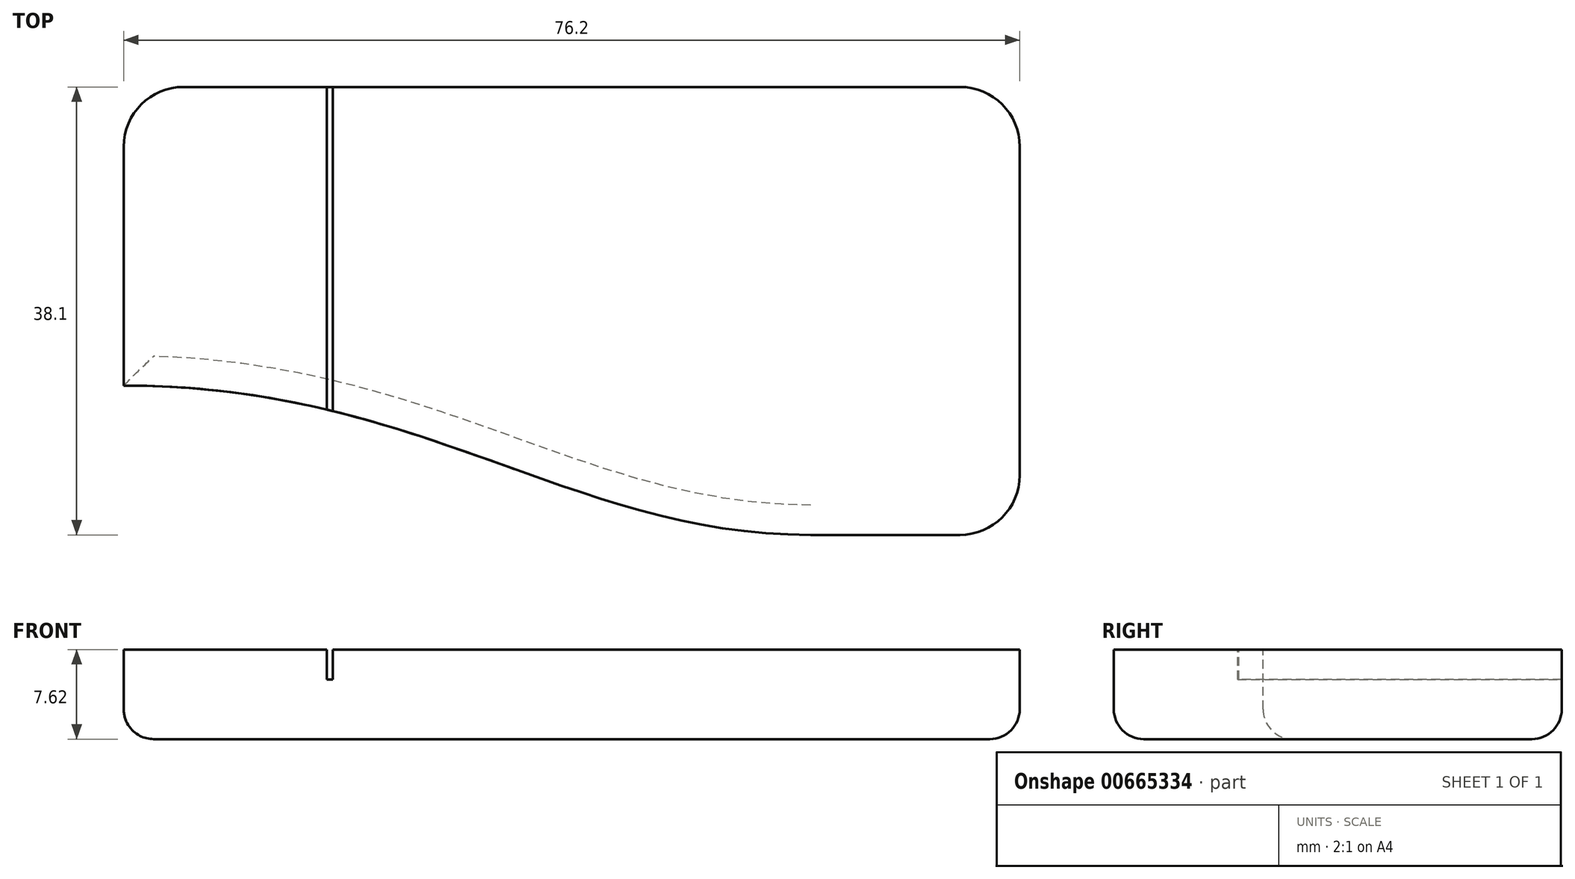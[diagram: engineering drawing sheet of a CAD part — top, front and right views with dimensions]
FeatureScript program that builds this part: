
annotation { "Feature Type Name" : "Feature", "Feature Type Description" : "" }
export const myFeature = defineFeature(function(context is Context, id is Id, definition is map)
    precondition{}
    {
        {
            var Q0;
            Q0=qCreatedBy(makeId("Top.planeOp"),FACE);
            var sketch = newSketch(context, id + "F0", { "sketchPlane" : qUnion([Q0])});
            skLineSegment(sketch, "E0.bottom", {"start": v(38.1, -19.05) * mm, "end": v(-38.1, -19.05) * mm});
            skLineSegment(sketch, "E0.top", {"start": v(38.1, 19.05) * mm, "end": v(-38.1, 19.05) * mm});
            skLineSegment(sketch, "E0.left", {"start": v(38.1, -19.05) * mm, "end": v(38.1, 19.05) * mm});
            skLineSegment(sketch, "E0.right", {"start": v(-38.1, -19.05) * mm, "end": v(-38.1, 19.05) * mm});
            skPoint(sketch, "E0.middle", {"position": v(0, 0) * mm});
            skSolve(sketch);
        }
        {
            var Q0;
            Q0=makeQuery(id+"F0.imprint","IMPRINT",FACE,{"disambiguationData":[TD([[makeQuery(id+"F0.imprint","IMPRINT",EDGE,{"derivedFrom":sQuery(id+"F0.wireOp",EDGE,"E0.bottom")}),-1.0]])]});
            extrude(context, id + "F1", {"entities" : qUnion([Q0]), "depth" : 7.62 * mm, "offsetDistance" : 25.4 * mm});
        }
        {
            var Q0;
            Q0=makeQuery(id+"F1.opExtrude","CAP_FACE",FACE,{"disambiguationData":[OSD([sQuery(id+"F0.wireOp",EDGE,"E0.bottom"),sQuery(id+"F0.wireOp",EDGE,"E0.top"),sQuery(id+"F0.wireOp",EDGE,"E0.left"),sQuery(id+"F0.wireOp",EDGE,"E0.right")])],"isStart":false});
            var sketch = newSketch(context, id + "F2", { "sketchPlane" : qUnion([Q0])});
            skLineSegment(sketch, "E1.bottom", {"start": v(20.32, -19.05) * mm, "end": v(-20.32, -19.05) * mm});
            skLineSegment(sketch, "E1.top", {"start": v(20.32, 19.05) * mm, "end": v(-20.32, 19.05) * mm});
            skLineSegment(sketch, "E1.left", {"start": v(20.32, -19.05) * mm, "end": v(20.32, 19.05) * mm});
            skLineSegment(sketch, "E1.right", {"start": v(-20.32, -19.05) * mm, "end": v(-20.32, 19.05) * mm});
            skPoint(sketch, "E1.middle", {"position": v(0, 0) * mm});
            skLineSegment(sketch, "E2.bottom", {"start": v(-20.32, 19.05) * mm, "end": v(-20.83, 19.05) * mm});
            skLineSegment(sketch, "E2.top", {"start": v(-20.32, -19.05) * mm, "end": v(-20.83, -19.05) * mm});
            skLineSegment(sketch, "E2.left", {"start": v(-20.32, 19.05) * mm, "end": v(-20.32, -19.05) * mm});
            skLineSegment(sketch, "E2.right", {"start": v(-20.83, 19.05) * mm, "end": v(-20.83, -19.05) * mm});
            skSolve(sketch);
        }
        {
            var Q0;
            {var subQ0=sQuery(id+"F2.wireOp",EDGE,"E1.left");Q0=makeQuery(id+"F2.imprint","IMPRINT",FACE,{"disambiguationData":[TD([[makeQuery(id+"F2.imprint","IMPRINT",EDGE,{"derivedFrom":subQ0}),-1.0]])]});}
            var sketch = newSketch(context, id + "F3", { "sketchPlane" : qUnion([Q0])});
            skLineSegment(sketch, "E3.0", {"start": v(-38.1, -19.05) * mm, "end": v(-38.1, 19.05) * mm});
            skFitSpline(sketch, "E4", {"points": [v(-38.1, -6.35) * mm, v(20.32, -19.05) * mm], "startDerivative": vector(76.2, 0) * mm, "endDerivative": vector(60.96, 0) * mm});
            skLineSegment(sketch, "E5.0", {"start": v(20.32, -19.05) * mm, "end": v(-20.32, -19.05) * mm});
            skLineSegment(sketch, "E6.0", {"start": v(20.32, -19.05) * mm, "end": v(-38.1, -19.05) * mm});
            skPoint(sketch, "E7.orphan", {"position": v(38.1, -19.05) * mm});
            skSolve(sketch);
        }
        {
            var Q0;
            {var subQ3=sQuery(id+"F3.wireOp",EDGE,"E4");Q0=makeQuery(id+"F3.imprint","IMPRINT",FACE,{"disambiguationData":[TD([[makeQuery(id+"F3.imprint","IMPRINT",EDGE,{"derivedFrom":subQ3}),-1.0]])]});}
            extrude(context, id + "F4", {"entities" : qUnion([Q0]), "operationType" : NewBodyOperationType.REMOVE, "endBound" : BoundingType.THROUGH_ALL, "oppositeDirection" : true, "depth" : 25.4 * mm, "offsetDistance" : 25.4 * mm});
        }
        {
            var Q0;
            Q0=makeQuery(id+"F4.boolean.opBoolean","COPY",EDGE,{"derivedFrom":makeQuery(id+"F4.opExtrude","SWEPT_EDGE",EDGE,{"disambiguationData":[OSD([sQuery(id+"F3.wireOp",EDGE,"E3.0"),sQuery(id+"F3.wireOp",EDGE,"E4")])]})});
            var Q1;
            Q1=makeQuery(id+"F1.opExtrude","SWEPT_EDGE",EDGE,{"disambiguationData":[OSD([sQuery(id+"F0.wireOp",EDGE,"E0.top"),sQuery(id+"F0.wireOp",EDGE,"E0.right")])]});
            var Q2;
            Q2=makeQuery(id+"F1.opExtrude","SWEPT_EDGE",EDGE,{"disambiguationData":[OSD([sQuery(id+"F0.wireOp",EDGE,"E0.bottom"),sQuery(id+"F0.wireOp",EDGE,"E0.left")])]});
            var Q3;
            Q3=makeQuery(id+"F1.opExtrude","SWEPT_EDGE",EDGE,{"disambiguationData":[OSD([sQuery(id+"F0.wireOp",EDGE,"E0.top"),sQuery(id+"F0.wireOp",EDGE,"E0.left")])]});
            fillet(context, id + "F5", {"entities" : qUnion([Q0, Q1, Q2, Q3]), "radius" : 5.08 * mm, "tangentPropagation" : true, "allowEdgeOverflow" : false});
        }
        {
            var Q0;
            Q0=makeQuery(id+"F4.boolean.opBoolean","COPY",EDGE,{"derivedFrom":makeQuery(id+"F4.opExtrude","CAP_EDGE",EDGE,{"disambiguationData":[OSD([sQuery(id+"F3.wireOp",EDGE,"E4")])],"isStart":true})});
            var Q1;
            Q1=makeQuery(id+"F4.boolean.opBoolean","INTERSECT",EDGE,{"derivedFrom":[makeQuery(id+"F1.opExtrude","CAP_FACE",FACE,{"disambiguationData":[OSD([sQuery(id+"F0.wireOp",EDGE,"E0.bottom"),sQuery(id+"F0.wireOp",EDGE,"E0.top"),sQuery(id+"F0.wireOp",EDGE,"E0.left"),sQuery(id+"F0.wireOp",EDGE,"E0.right")])],"isStart":true}),makeQuery(id+"F4.opExtrude","SWEPT_FACE",FACE,{"disambiguationData":[OSD([sQuery(id+"F3.wireOp",EDGE,"E4")])]})]});
            fillet(context, id + "F6", {"entities" : qUnion([Q0, Q1]), "radius" : 2.54 * mm, "tangentPropagation" : true, "allowEdgeOverflow" : false});
        }
        {
            var Q0;
            Q0=makeQuery(id+"F2.imprint","IMPRINT",FACE,{"disambiguationData":[TD([[makeQuery(id+"F2.imprint","IMPRINT",EDGE,{"derivedFrom":sQuery(id+"F2.wireOp",EDGE,"E2.bottom")}),1.0]])]});
            extrude(context, id + "F7", {"entities" : qUnion([Q0]), "operationType" : NewBodyOperationType.REMOVE, "oppositeDirection" : true, "depth" : 2.54 * mm, "offsetDistance" : 25.4 * mm});
        }
    });
